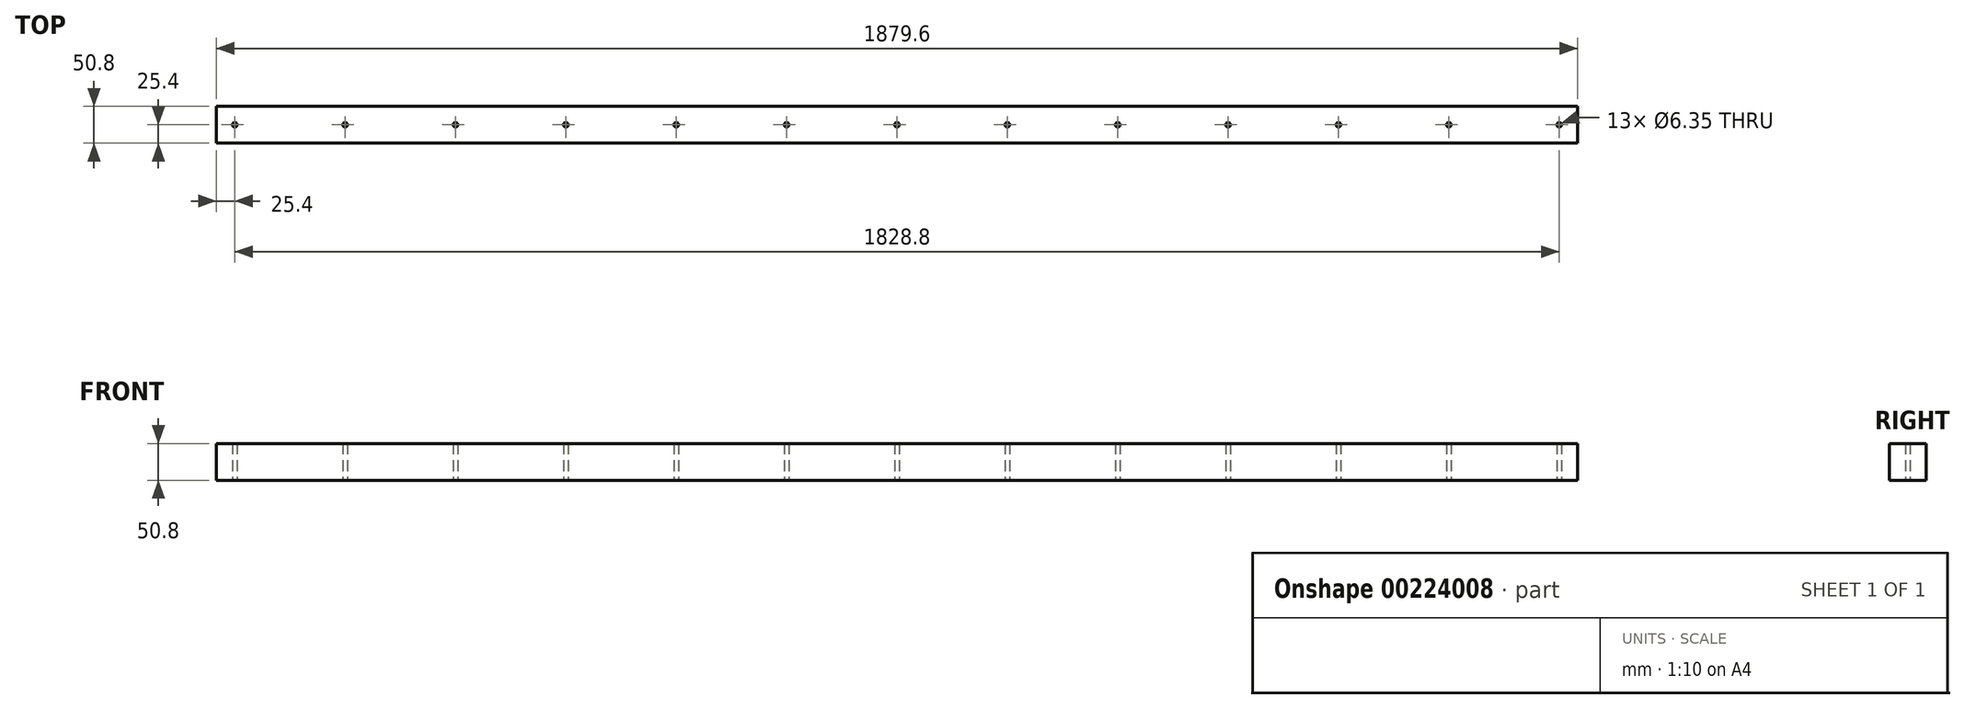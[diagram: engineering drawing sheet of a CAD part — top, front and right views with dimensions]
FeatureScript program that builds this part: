
annotation { "Feature Type Name" : "Feature", "Feature Type Description" : "" }
export const myFeature = defineFeature(function(context is Context, id is Id, definition is map)
    precondition{}
    {
        {
            var Q0;
            Q0=qCreatedBy(makeId("Top.planeOp"),FACE);
            var sketch = newSketch(context, id + "F0", { "sketchPlane" : qUnion([Q0])});
            skLineSegment(sketch, "E0.bottom", {"start": v(0, 0) * mm, "end": v(1879.6, 0) * mm});
            skLineSegment(sketch, "E0.top", {"start": v(0, 50.8) * mm, "end": v(1879.6, 50.8) * mm});
            skLineSegment(sketch, "E0.left", {"start": v(0, 0) * mm, "end": v(0, 50.8) * mm});
            skLineSegment(sketch, "E0.right", {"start": v(1879.6, 0) * mm, "end": v(1879.6, 50.8) * mm});
            skCircle(sketch, "E1", {"center": v(25.4, 25.4) * mm, "radius": 3.18 * mm});
            skCircle(sketch, "E2", {"center": v(1854.2, 25.4) * mm, "radius": 3.18 * mm});
            skCircle(sketch, "E3", {"center": v(177.8, 25.4) * mm, "radius": 3.18 * mm});
            skCircle(sketch, "E4.1.0.0", {"center": v(330.2, 25.4) * mm, "radius": 3.18 * mm});
            skCircle(sketch, "E4.2.0.0", {"center": v(482.6, 25.4) * mm, "radius": 3.18 * mm});
            skCircle(sketch, "E4.3.0.0", {"center": v(635, 25.4) * mm, "radius": 3.18 * mm});
            skCircle(sketch, "E4.4.0.0", {"center": v(787.4, 25.4) * mm, "radius": 3.18 * mm});
            skCircle(sketch, "E4.5.0.0", {"center": v(939.8, 25.4) * mm, "radius": 3.18 * mm});
            skCircle(sketch, "E4.6.0.0", {"center": v(1092.2, 25.4) * mm, "radius": 3.18 * mm});
            skCircle(sketch, "E4.7.0.0", {"center": v(1244.6, 25.4) * mm, "radius": 3.18 * mm});
            skCircle(sketch, "E4.8.0.0", {"center": v(1397, 25.4) * mm, "radius": 3.18 * mm});
            skCircle(sketch, "E4.9.0.0", {"center": v(1549.4, 25.4) * mm, "radius": 3.18 * mm});
            skCircle(sketch, "E4.10.0.0", {"center": v(1701.8, 25.4) * mm, "radius": 3.18 * mm});
            skLineSegment(sketch, "E4.direction1", {"start": v(177.8, 25.4) * mm, "end": v(330.2, 25.4) * mm, "construction": true});
            skSolve(sketch);
        }
        {
            var Q0;
            Q0=makeQuery(id+"F0.imprint","IMPRINT",FACE,{"disambiguationData":[TD([[makeQuery(id+"F0.imprint","IMPRINT",EDGE,{"derivedFrom":sQuery(id+"F0.wireOp",EDGE,"E0.bottom")}),1.0]])]});
            extrude(context, id + "F1", {"entities" : qUnion([Q0]), "depth" : 50.8 * mm});
        }
    });
